# Revit family: Time Power 50 K-70 K singola
name_source: partatom
category: Attrezzatura meccanica
units: mm (PartAtom-declared; Revit-internal decimal feet)

## family parameters
Basato su piano di lavoro = No
Classificazione = Nessuno
Condiviso = Sì
Punto di calcolo locali = No
Quota connettore circolare = Usa diametro
Sempre verticale = Sì
Taglio con vuoti quando caricato = No
Tipo di parte = Normale

## types (2) — shared parameters
Date of publishing = 08/06/2020
Depth = 475 mm  [stored 1.5584 ft]
Descrizione = Condensing thermal module
Design country = Italy
Energetic efficiency (92/42/CEE) = n.d.
Flue outlet = 100 mm  [stored 0.328084 ft]
Gas Inlet Diameter = 25 mm  [stored 0.082021 ft]
Height = 837 mm  [stored 2.74606 ft]
Hydronic Return Diameter = 32 mm  [stored 0.104987 ft]
Hydronic Supply Diameter = 32 mm  [stored 0.104987 ft]
IFC Classification = Boiler
Manufacturer country = Italy
Manufacturer name = Italtherm S.p.A.
Material main = Metal
Material secondary = Plastic
Max number in cascade = 4
Modello = Time Power K
NBS reference Description = Condensing boilers
Omniclass Description = Condensing boilers
Power supply | Frequency (Hz) = 50 Hz
Power supply | Phase = 1
Power supply | Voltage (V) = 230 V
Product certification = 0476CQ1281
Product family = High efficiency condensing systems
Product group = Boilers for commercial applications
Produttore = Italtherm
Siphon with condensate drain = 25 mm  [stored 0.082021 ft]
URL = https://www.italtherm.it
URL ENG = https://en.italtherm.it
Uniclass 2015 Name = Boilers
Width = 450 mm  [stored 1.47638 ft]
zero-valued in all types: Edition number, Prospetto di default

## per-type parameters (varying)
| type | Codice assieme | EAN code | Efficiency 30% | Maximum heat output 50/30°C | Maximum heat output 80/60°C | Maximum heating heat input | Minimum heat output 50/30°C | Minimum heat output 80/60°C | Nominal efficiency 50/30°C | Nominal efficiency 80/60°C | Power consumption (W) | Weight |
| 50 K | 301001210 | 8059616962464 | 106.7% | 49.2 kW | 46 kW | 47.5 kW | 5.2 kW | 4.7 kW | 103.5% | 96.8% | 145 W | 38.80 kg |
| 70 K | 301001212 | 8059616962488 | 107.2% | 65.6 kW | 61.1 kW | 63 kW | 7.3 kW | 6.6 kW | 104.1% | 97% | 190 W | 45.80 kg |

note: [stored X ft] marks values corroborated as IEEE doubles in the binary element streams (Revit-internal decimal feet)
